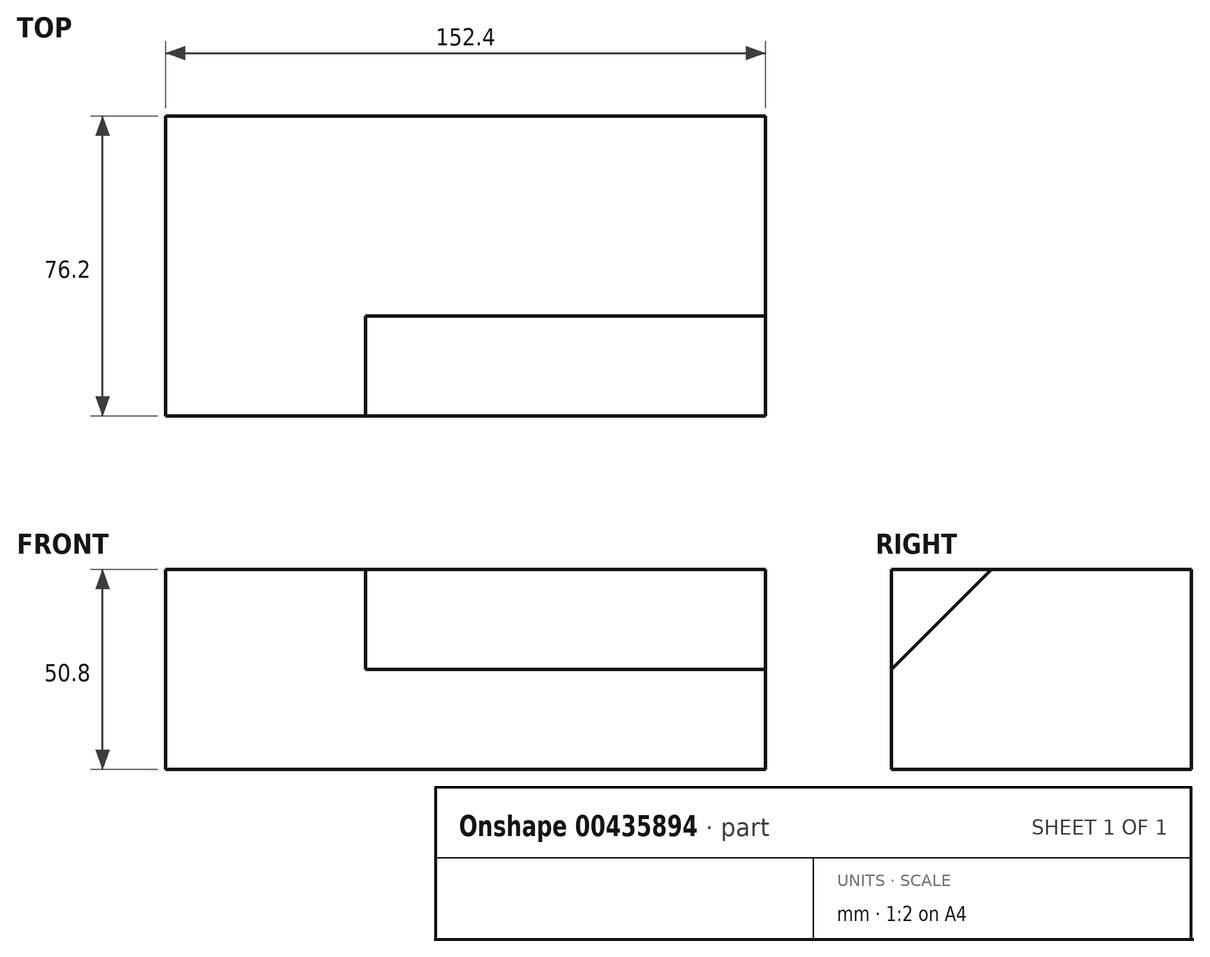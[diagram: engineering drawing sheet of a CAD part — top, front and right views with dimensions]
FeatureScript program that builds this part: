
annotation { "Feature Type Name" : "Feature", "Feature Type Description" : "" }
export const myFeature = defineFeature(function(context is Context, id is Id, definition is map)
    precondition{}
    {
        {
            var Q0;
            Q0=qCreatedBy(makeId("Front.planeOp"),FACE);
            var sketch = newSketch(context, id + "F0", { "sketchPlane" : qUnion([Q0])});
            skLineSegment(sketch, "E0", {"start": v(0, 0) * mm, "end": v(152.4, 0) * mm});
            skLineSegment(sketch, "E1", {"start": v(0, 0) * mm, "end": v(0, 50.8) * mm});
            skLineSegment(sketch, "E2", {"start": v(152.4, 0) * mm, "end": v(152.4, 50.8) * mm});
            skLineSegment(sketch, "E3", {"start": v(0, 50.8) * mm, "end": v(152.4, 50.8) * mm});
            skSolve(sketch);
        }
        {
            var Q0;
            Q0=makeQuery(id+"F0.imprint","IMPRINT",FACE,{"disambiguationData":[TD([[makeQuery(id+"F0.imprint","IMPRINT",EDGE,{"derivedFrom":sQuery(id+"F0.wireOp",EDGE,"E0")}),1.0]])]});
            extrude(context, id + "F1", {"entities" : qUnion([Q0]), "oppositeDirection" : true, "depth" : 76.2 * mm});
        }
        {
            var Q0;
            Q0=makeQuery(id+"F1.opExtrude","SWEPT_FACE",FACE,{"disambiguationData":[OSD([sQuery(id+"F0.wireOp",EDGE,"E2")])]});
            var sketch = newSketch(context, id + "F2", { "sketchPlane" : qUnion([Q0])});
            skLineSegment(sketch, "E4", {"start": v(0, 50.8) * mm, "end": v(25.4, 50.8) * mm});
            skLineSegment(sketch, "E5", {"start": v(25.4, 50.8) * mm, "end": v(0, 25.4) * mm});
            skLineSegment(sketch, "E6", {"start": v(0, 25.4) * mm, "end": v(0, 50.8) * mm});
            skSolve(sketch);
        }
        {
            var Q0;
            Q0=makeQuery(id+"F2.imprint","IMPRINT",FACE,{"disambiguationData":[TD([[makeQuery(id+"F2.imprint","IMPRINT",EDGE,{"derivedFrom":sQuery(id+"F2.wireOp",EDGE,"E4")}),1.0]])]});
            extrude(context, id + "F3", {"entities" : qUnion([Q0]), "operationType" : NewBodyOperationType.REMOVE, "oppositeDirection" : true, "depth" : 101.6 * mm});
        }
    });
